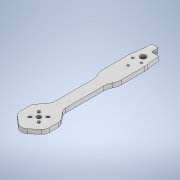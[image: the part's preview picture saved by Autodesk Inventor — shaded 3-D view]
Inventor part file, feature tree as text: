
AUTODESK INVENTOR PART (.ipt)
format: ipt  version: 2020 (Build 240168000, 168)  size: 180,224 bytes
history: native  units: mm
features: extrude x1, sketch x1
ambient origin geometry x8: Origin, YZ Plane, XZ Plane, XY Plane, X Axis, Y Axis, Z Axis, Center Point
bodies: Solid1 (feature_tree)
feature tree (2):
  extrude  "Extrusion1"  [1 undecoded]
  sketch  "Sketch1"  dims[d0=6.0mm d1=0.0mm]
note: 1 required parameter value undecoded (feature->parameter linkage not recoverable at this tier; creation-order binding heuristic only, values carry confidence <= 0.55)
